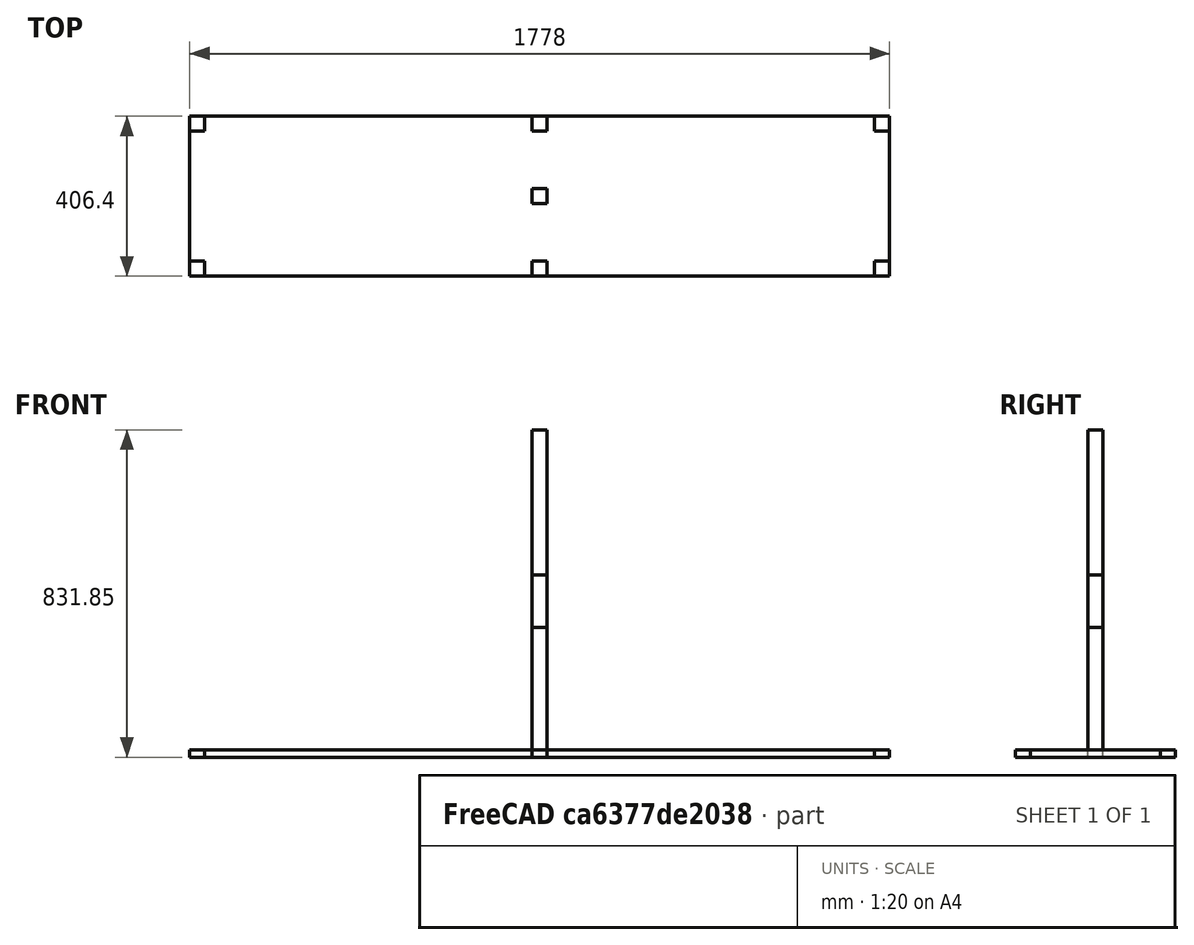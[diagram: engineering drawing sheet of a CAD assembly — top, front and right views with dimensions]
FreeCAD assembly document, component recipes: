
FREECAD ASSEMBLY — COMPONENT RECIPES ("tv_console")

This assembly document has 22 components, labeled P0..P21 below (a component is one placed body or linked part). 22 of them carry a construction recipe — the FreeCAD feature program that regenerates the part from scratch, quoted from this document or its linked companion documents; the rest are supplied as boundary geometry only. No exploded tour is included for this assembly.
COMPONENT P0 — recipe-attached ("leg", modeled in this document).
Construction recipe (the document's own serialized feature program — sketch geometry with constraints, then the solid features built on it; lengths are millimeters unless a unit is written):

FEATURE [Sketcher::SketchObject] Sketch001
  ArcFitTolerance = 0
  AttachmentSupport = -> [XY_Plane001]
  ExternalTypes = [0]
  FullyConstrained = true
  MakeInternals = false
  MapMode = 5
  sketch-geometry (5):
    g0: LineSegment StartX=-19.05 StartY=-19.05 StartZ=0 EndX=19.05 EndY=-19.05 EndZ=0
    g1: LineSegment StartX=19.05 StartY=-19.05 StartZ=0 EndX=19.05 EndY=19.05 EndZ=0
    g2: LineSegment StartX=19.05 StartY=19.05 StartZ=0 EndX=-19.05 EndY=19.05 EndZ=0
    g3: LineSegment StartX=-19.05 StartY=19.05 StartZ=0 EndX=-19.05 EndY=-19.05 EndZ=0
    g4: GeomPoint [constr] X=0 Y=0 Z=0
  constraints (12):
    c: Coincident(g0,g1)
    c: Coincident(g1,g2)
    c: Coincident(g2,g3)
    c: Coincident(g3,g0)
    c: Horizontal(g0)
    c: Horizontal(g2)
    c: Vertical(g1)
    c: Vertical(g3)
    c: Symmetric(g2,g0,g4)
    c: Distance(g1,g3) = 38.1
    c: Distance(g0,g2) = 38.1
    c: Coincident(g4,g-1)
FEATURE [PartDesign::Pad] Pad001
  Direction = (0,0,1)
  Length = 463.55
  Length2 = 10
  Profile = -> Sketch001
  ReferenceAxis = -> Sketch001 [N_Axis]
  Suppressed = false
  Type = 0
  expr: Length = 19 " - Spreadsheet.plywood_thickness
FEATURE [PartDesign::Body] Body001  label="leg"
  AllowCompound = false
  Group = -> [Sketch001,Pad001]
  Origin = -> Origin001
  Tip = -> Pad001
COMPONENT P1 — same part as P0; its construction recipe is shown at P0.
COMPONENT P2 — same part as P0; its construction recipe is shown at P0.
COMPONENT P3 — same part as P0; its construction recipe is shown at P0.
COMPONENT P4 — same part as P0; its construction recipe is shown at P0.
COMPONENT P5 — same part as P0; its construction recipe is shown at P0.
COMPONENT P6 — recipe-attached ("long support001", modeled in this document).
Construction recipe (the document's own serialized feature program — sketch geometry with constraints, then the solid features built on it; lengths are millimeters unless a unit is written):

FEATURE [Sketcher::SketchObject] Sketch003
  ArcFitTolerance = 0
  AttachmentSupport = -> [XY_Plane004]
  ExternalTypes = [0]
  FullyConstrained = true
  MakeInternals = false
  MapMode = 5
  sketch-geometry (5):
    g0: LineSegment StartX=-19.05 StartY=-19.05 StartZ=0 EndX=19.05 EndY=-19.05 EndZ=0
    g1: LineSegment StartX=19.05 StartY=-19.05 StartZ=0 EndX=19.05 EndY=19.05 EndZ=0
    g2: LineSegment StartX=19.05 StartY=19.05 StartZ=0 EndX=-19.05 EndY=19.05 EndZ=0
    g3: LineSegment StartX=-19.05 StartY=19.05 StartZ=0 EndX=-19.05 EndY=-19.05 EndZ=0
    g4: GeomPoint [constr] X=0 Y=0 Z=0
  constraints (12):
    c: Coincident(g0,g1)
    c: Coincident(g1,g2)
    c: Coincident(g2,g3)
    c: Coincident(g3,g0)
    c: Horizontal(g0)
    c: Horizontal(g2)
    c: Vertical(g1)
    c: Vertical(g3)
    c: Symmetric(g2,g0,g4)
    c: Distance(g1,g3) = 38.1
    c: Distance(g0,g2) = 38.1
    c: Coincident(g4,g-1)
FEATURE [PartDesign::Pad] Pad003
  Direction = (0,0,1)
  Length = 831.85
  Length2 = 10
  Profile = -> Sketch003
  ReferenceAxis = -> Sketch003 [N_Axis]
  Suppressed = false
  Type = 0
  expr: Length = 35 " - 2.25 "
FEATURE [PartDesign::Body] Body004  label="long support"
  AllowCompound = false
  Group = -> [Sketch003,Pad003]
  Origin = -> Origin004
  Tip = -> Pad003
COMPONENT P7 — same part as P6; its construction recipe is shown at P6.
COMPONENT P8 — same part as P6; its construction recipe is shown at P6.
COMPONENT P9 — same part as P6; its construction recipe is shown at P6.
COMPONENT P10 — same part as P6; its construction recipe is shown at P6.
COMPONENT P11 — same part as P6; its construction recipe is shown at P6.
COMPONENT P12 — same part as P6; its construction recipe is shown at P6.
COMPONENT P13 — same part as P6; its construction recipe is shown at P6.
COMPONENT P14 — recipe-attached ("shelf", modeled in this document).
Construction recipe (the document's own serialized feature program — sketch geometry with constraints, then the solid features built on it; lengths are millimeters unless a unit is written):

FEATURE [Sketcher::SketchObject] Sketch002
  ArcFitTolerance = 0
  AttachmentSupport = -> [XY_Plane002]
  ExternalTypes = [0]
  FullyConstrained = false
  MakeInternals = false
  MapMode = 5
  sketch-geometry (24):
    g0: LineSegment StartX=0 StartY=165.1 StartZ=0 EndX=19.05 EndY=165.1 EndZ=0
    g1: LineSegment StartX=19.05 StartY=165.1 StartZ=0 EndX=19.05 EndY=203.2 EndZ=0
    g2: LineSegment StartX=19.05 StartY=203.2 StartZ=0 EndX=850.9 EndY=203.2 EndZ=0
    g3: LineSegment StartX=850.9 StartY=203.2 StartZ=0 EndX=850.9 EndY=165.1 EndZ=0
    g4: LineSegment StartX=850.9 StartY=165.1 StartZ=0 EndX=889 EndY=165.1 EndZ=0
    g5: LineSegment StartX=889 StartY=165.1 StartZ=0 EndX=889 EndY=0 EndZ=0
    g6: LineSegment StartX=0 StartY=-165.1 StartZ=0 EndX=19.05 EndY=-165.1 EndZ=0
    g7: LineSegment StartX=19.05 StartY=-165.1 StartZ=0 EndX=19.05 EndY=-203.2 EndZ=0
    g8: LineSegment StartX=19.05 StartY=-203.2 StartZ=0 EndX=850.9 EndY=-203.2 EndZ=0
    g9: LineSegment StartX=850.9 StartY=-203.2 StartZ=0 EndX=850.9 EndY=-165.1 EndZ=0
    g10: LineSegment StartX=850.9 StartY=-165.1 StartZ=0 EndX=889 EndY=-165.1 EndZ=0
    g11: LineSegment StartX=889 StartY=-165.1 StartZ=0 EndX=889 EndY=0 EndZ=0
    g12: LineSegment StartX=0 StartY=165.1 StartZ=0 EndX=-19.05 EndY=165.1 EndZ=0
    g13: LineSegment StartX=-19.05 StartY=165.1 StartZ=0 EndX=-19.05 EndY=203.2 EndZ=0
    g14: LineSegment StartX=-19.05 StartY=203.2 StartZ=0 EndX=-850.9 EndY=203.2 EndZ=0
    g15: LineSegment StartX=-850.9 StartY=203.2 StartZ=0 EndX=-850.9 EndY=165.1 EndZ=0
    g16: LineSegment StartX=-850.9 StartY=165.1 StartZ=0 EndX=-889 EndY=165.1 EndZ=0
    g17: LineSegment StartX=-889 StartY=165.1 StartZ=0 EndX=-889 EndY=0 EndZ=0
    g18: LineSegment StartX=0 StartY=-165.1 StartZ=0 EndX=-19.05 EndY=-165.1 EndZ=0
    g19: LineSegment StartX=-19.05 StartY=-165.1 StartZ=0 EndX=-19.05 EndY=-203.2 EndZ=0
    g20: LineSegment StartX=-19.05 StartY=-203.2 StartZ=0 EndX=-850.9 EndY=-203.2 EndZ=0
    g21: LineSegment StartX=-850.9 StartY=-203.2 StartZ=0 EndX=-850.9 EndY=-165.1 EndZ=0
    g22: LineSegment StartX=-850.9 StartY=-165.1 StartZ=0 EndX=-889 EndY=-165.1 EndZ=0
    g23: LineSegment StartX=-889 StartY=-165.1 StartZ=0 EndX=-889 EndY=0 EndZ=0
  constraints (58):
    c: PointOnObject(g0,g-2)
    c: Horizontal(g0)
    c: Coincident(g0,g1)
    c: Vertical(g1)
    c: Coincident(g1,g2)
    c: Horizontal(g2)
    c: Coincident(g2,g3)
    c: Vertical(g3)
    c: Coincident(g3,g4)
    c: Horizontal(g4)
    c: Coincident(g4,g5)
    c: PointOnObject(g5,g-1)
    c: Vertical(g5)
    c: DistanceY(g1,g1) = 38.1
    c: DistanceX(g0,g0) = 19.05
    c: Equal(g3,g1)
    c: DistanceY(g5,g2) = 203.2
    c: DistanceX(g0,g4) = 889
    c: Equal(g4,g3)
    c: Horizontal(g6)
    c: Coincident(g6,g7)
    c: Vertical(g7)
    c: Coincident(g7,g8)
    c: Horizontal(g8)
    c: Coincident(g8,g9)
    c: Vertical(g9)
    c: Coincident(g9,g10)
    c: Horizontal(g10)
    c: Coincident(g10,g11)
    c: Vertical(g11)
    c: Equal(g9,g7)
    c: Equal(g10,g9)
    c: Horizontal(g12)
    c: Coincident(g12,g13)
    c: Vertical(g13)
    c: Coincident(g13,g14)
    c: Horizontal(g14)
    c: Coincident(g14,g15)
    c: Vertical(g15)
    c: Coincident(g15,g16)
    c: Horizontal(g16)
    c: Coincident(g16,g17)
    c: Vertical(g17)
    c: Equal(g15,g13)
    c: Equal(g16,g15)
    c: Horizontal(g18)
    c: Coincident(g18,g19)
    c: Vertical(g19)
    c: Coincident(g19,g20)
    c: Horizontal(g20)
    c: Coincident(g20,g21)
    c: Vertical(g21)
    c: Coincident(g21,g22)
    c: Horizontal(g22)
    c: Coincident(g22,g23)
    c: Vertical(g23)
    c: Equal(g21,g19)
    c: Equal(g22,g21)
FEATURE [PartDesign::Pad] Pad002
  Direction = (0,0,1)
  Length = 19.05
  Length2 = 10
  Profile = -> Sketch002
  ReferenceAxis = -> Sketch002 [N_Axis]
  Suppressed = false
  Type = 0
  expr: Length = Spreadsheet.plywood_thickness
FEATURE [PartDesign::Body] Body002  label="shelf"
  AllowCompound = false
  Group = -> [Sketch002,Pad002]
  Origin = -> Origin002
  Tip = -> Pad002
COMPONENT P15 — recipe-attached ("short support001", modeled in this document).
Construction recipe (the document's own serialized feature program — sketch geometry with constraints, then the solid features built on it; lengths are millimeters unless a unit is written):

FEATURE [Sketcher::SketchObject] Sketch004
  ArcFitTolerance = 0
  AttachmentSupport = -> [XY_Plane005]
  ExternalTypes = [0]
  FullyConstrained = true
  MakeInternals = false
  MapMode = 5
  sketch-geometry (5):
    g0: LineSegment StartX=-19.05 StartY=-19.05 StartZ=0 EndX=19.05 EndY=-19.05 EndZ=0
    g1: LineSegment StartX=19.05 StartY=-19.05 StartZ=0 EndX=19.05 EndY=19.05 EndZ=0
    g2: LineSegment StartX=19.05 StartY=19.05 StartZ=0 EndX=-19.05 EndY=19.05 EndZ=0
    g3: LineSegment StartX=-19.05 StartY=19.05 StartZ=0 EndX=-19.05 EndY=-19.05 EndZ=0
    g4: GeomPoint [constr] X=0 Y=0 Z=0
  constraints (12):
    c: Coincident(g0,g1)
    c: Coincident(g1,g2)
    c: Coincident(g2,g3)
    c: Coincident(g3,g0)
    c: Horizontal(g0)
    c: Horizontal(g2)
    c: Vertical(g1)
    c: Vertical(g3)
    c: Symmetric(g2,g0,g4)
    c: Distance(g1,g3) = 38.1
    c: Distance(g0,g2) = 38.1
    c: Coincident(g4,g-1)
FEATURE [PartDesign::Pad] Pad004
  Direction = (0,0,1)
  Length = 330.2
  Length2 = 10
  Profile = -> Sketch004
  ReferenceAxis = -> Sketch004 [N_Axis]
  Suppressed = false
  Type = 0
  expr: Length = 13 "
FEATURE [PartDesign::Body] Body005  label="short support"
  AllowCompound = false
  Group = -> [Sketch004,Pad004]
  Origin = -> Origin005
  Tip = -> Pad004
COMPONENT P16 — same part as P15; its construction recipe is shown at P15.
COMPONENT P17 — same part as P15; its construction recipe is shown at P15.
COMPONENT P18 — same part as P15; its construction recipe is shown at P15.
COMPONENT P19 — same part as P15; its construction recipe is shown at P15.
COMPONENT P20 — same part as P15; its construction recipe is shown at P15.
COMPONENT P21 — recipe-attached ("top", modeled in this document).
Construction recipe (the document's own serialized feature program — sketch geometry with constraints, then the solid features built on it; lengths are millimeters unless a unit is written):

FEATURE [Sketcher::SketchObject] Sketch
  ArcFitTolerance = 0
  AttachmentSupport = -> [XY_Plane]
  ExternalTypes = [0]
  FullyConstrained = true
  MakeInternals = false
  MapMode = 5
  sketch-geometry (5):
    g0: LineSegment StartX=-889 StartY=-203.2 StartZ=0 EndX=889 EndY=-203.2 EndZ=0
    g1: LineSegment StartX=889 StartY=-203.2 StartZ=0 EndX=889 EndY=203.2 EndZ=0
    g2: LineSegment StartX=889 StartY=203.2 StartZ=0 EndX=-889 EndY=203.2 EndZ=0
    g3: LineSegment StartX=-889 StartY=203.2 StartZ=0 EndX=-889 EndY=-203.2 EndZ=0
    g4: GeomPoint [constr] X=0 Y=0 Z=0
  constraints (12):
    c: Coincident(g0,g1)
    c: Coincident(g1,g2)
    c: Coincident(g2,g3)
    c: Coincident(g3,g0)
    c: Horizontal(g0)
    c: Horizontal(g2)
    c: Vertical(g1)
    c: Vertical(g3)
    c: Symmetric(g2,g0,g4)
    c: Distance(g1,g3) = 1778
    c: Distance(g0,g2) = 406.4
    c: Coincident(g4,g-1)
FEATURE [PartDesign::Pad] Pad
  Direction = (0,0,1)
  Length = 19.05
  Length2 = 10
  Profile = -> Sketch
  ReferenceAxis = -> Sketch [N_Axis]
  Suppressed = false
  Type = 0
  expr: Length = Spreadsheet.plywood_thickness
FEATURE [PartDesign::Body] Body  label="top"
  AllowCompound = false
  Group = -> [Sketch,Pad]
  Origin = -> Origin
  Tip = -> Pad
PROVENANCE & LICENSES
A FreeCAD (.FCStd) document from a public repository crawl; recipes are the document's own serialized feature recipes (and, for linked parts, companion documents' recipes).
License: as declared in the source repository (recorded in the dataset sidecar).
